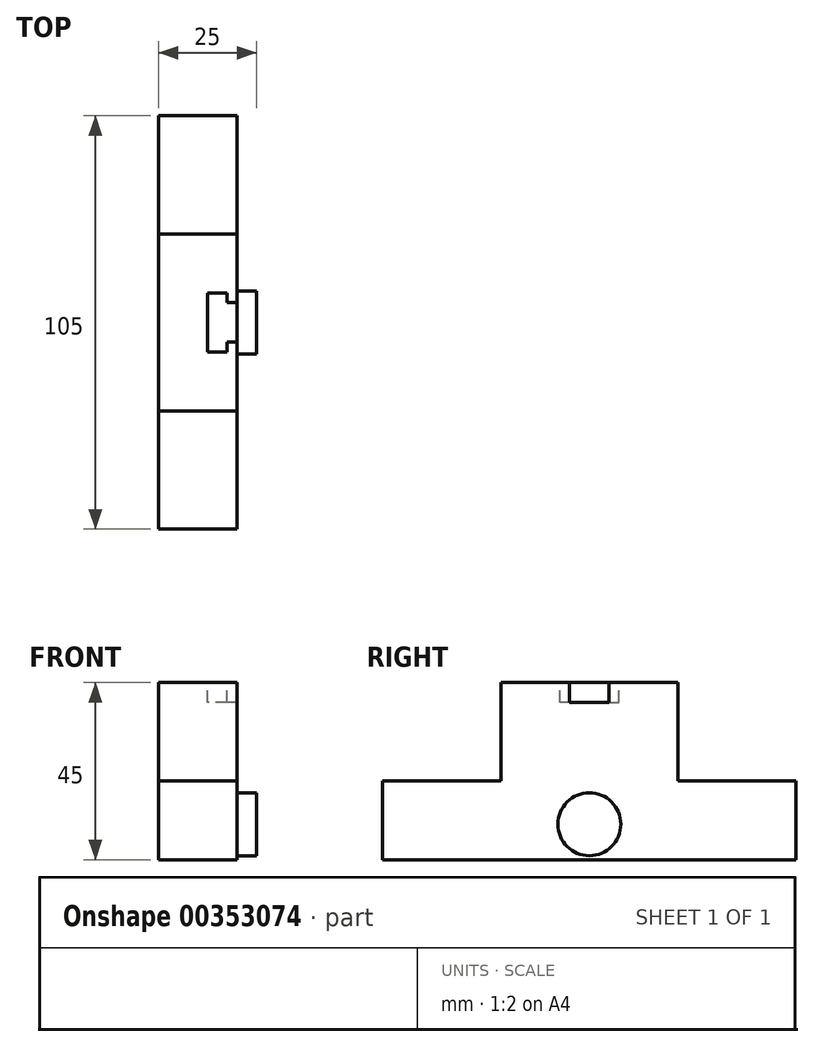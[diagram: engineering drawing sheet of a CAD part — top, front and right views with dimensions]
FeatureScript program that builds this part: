
annotation { "Feature Type Name" : "Feature", "Feature Type Description" : "" }
export const myFeature = defineFeature(function(context is Context, id is Id, definition is map)
    precondition{}
    {
        {
            var Q0;
            Q0=qCreatedBy(makeId("Top.planeOp"),FACE);
            var sketch = newSketch(context, id + "F0", { "sketchPlane" : qUnion([Q0])});
            skLineSegment(sketch, "E0.bottom", {"start": v(0, 0) * mm, "end": v(-20, 0) * mm});
            skLineSegment(sketch, "E0.top", {"start": v(0, 45) * mm, "end": v(-20, 45) * mm});
            skLineSegment(sketch, "E0.left", {"start": v(0, 0) * mm, "end": v(0, 45) * mm});
            skLineSegment(sketch, "E0.right", {"start": v(-20, 0) * mm, "end": v(-20, 45) * mm});
            skSolve(sketch);
        }
        {
            var Q0;
            Q0=makeQuery(id+"F0.imprint","IMPRINT",FACE,{"disambiguationData":[TD([[makeQuery(id+"F0.imprint","IMPRINT",EDGE,{"derivedFrom":sQuery(id+"F0.wireOp",EDGE,"E0.bottom")}),-1.0]])]});
            extrude(context, id + "F1", {"entities" : qUnion([Q0]), "depth" : 45 * mm});
        }
        {
            var Q0;
            Q0=makeQuery(id+"F1.opExtrude","CAP_FACE",FACE,{"disambiguationData":[OSD([sQuery(id+"F0.wireOp",EDGE,"E0.bottom"),sQuery(id+"F0.wireOp",EDGE,"E0.top"),sQuery(id+"F0.wireOp",EDGE,"E0.left"),sQuery(id+"F0.wireOp",EDGE,"E0.right")])],"isStart":false});
            var sketch = newSketch(context, id + "F2", { "sketchPlane" : qUnion([Q0])});
            skLineSegment(sketch, "E1", {"start": v(0, 22.5) * mm, "end": v(-20, 22.5) * mm, "construction": true});
            skLineSegment(sketch, "E2", {"start": v(0, 22.5) * mm, "end": v(0, 27.5) * mm, "construction": true});
            skLineSegment(sketch, "E3", {"start": v(0, 27.5) * mm, "end": v(-2.5, 27.5) * mm});
            skLineSegment(sketch, "E4", {"start": v(-2.5, 27.5) * mm, "end": v(-2.5, 30) * mm});
            skLineSegment(sketch, "E5", {"start": v(-2.5, 30) * mm, "end": v(-7.5, 30) * mm});
            skLineSegment(sketch, "E6", {"start": v(-7.5, 30) * mm, "end": v(-7.5, 15) * mm});
            skLineSegment(sketch, "E7", {"start": v(-7.5, 15) * mm, "end": v(-2.5, 15) * mm});
            skLineSegment(sketch, "E8", {"start": v(-2.5, 15) * mm, "end": v(-2.5, 17.5) * mm});
            skLineSegment(sketch, "E9", {"start": v(-2.5, 17.5) * mm, "end": v(0, 17.5) * mm});
            skSolve(sketch);
        }
        {
            var Q0;
            {var subQ0=sQuery(id+"F2.wireOp",EDGE,"E3");Q0=makeQuery(id+"F2.imprint","IMPRINT",FACE,{"disambiguationData":[TD([[makeQuery(id+"F2.imprint","IMPRINT",EDGE,{"derivedFrom":subQ0}),1.0]])]});}
            extrude(context, id + "F3", {"entities" : qUnion([Q0]), "operationType" : NewBodyOperationType.REMOVE, "oppositeDirection" : true, "depth" : 5 * mm});
        }
        {
            var Q0;
            Q0=makeQuery(id+"F1.opExtrude","SWEPT_FACE",FACE,{"disambiguationData":[OSD([sQuery(id+"F0.wireOp",EDGE,"E0.left")])]});
            var sketch = newSketch(context, id + "F4", { "sketchPlane" : qUnion([Q0])});
            skPoint(sketch, "E10.endSnap0", {"position": v(22.5, 0) * mm});
            skLineSegment(sketch, "E11", {"start": v(22.5, 0) * mm, "end": v(22.5, 9) * mm, "construction": true});
            skCircle(sketch, "E12", {"center": v(22.5, 9) * mm, "radius": 8 * mm});
            skSolve(sketch);
        }
        {
            var Q0;
            Q0=makeQuery(id+"F4.imprint","IMPRINT",FACE,{"disambiguationData":[TD([[makeQuery(id+"F4.imprint","IMPRINT",EDGE,{"derivedFrom":sQuery(id+"F4.wireOp",EDGE,"E12")}),1.0]])]});
            extrude(context, id + "F5", {"entities" : qUnion([Q0]), "operationType" : NewBodyOperationType.ADD, "depth" : 5 * mm});
        }
        {
            var Q0;
            Q0=makeQuery(id+"F1.opExtrude","SWEPT_FACE",FACE,{"disambiguationData":[OSD([sQuery(id+"F0.wireOp",EDGE,"E0.bottom")])]});
            var sketch = newSketch(context, id + "F6", { "sketchPlane" : qUnion([Q0])});
            skLineSegment(sketch, "E13", {"start": v(0, 0) * mm, "end": v(0, 20) * mm});
            skLineSegment(sketch, "E14", {"start": v(0, 20) * mm, "end": v(-20, 20) * mm});
            skLineSegment(sketch, "E15", {"start": v(-20, 20) * mm, "end": v(-20, 0) * mm});
            skLineSegment(sketch, "E16", {"start": v(-20, 0) * mm, "end": v(0, 0) * mm});
            skSolve(sketch);
        }
        {
            var Q0;
            Q0=makeQuery(id+"F6.imprint","IMPRINT",FACE,{"disambiguationData":[TD([[makeQuery(id+"F6.imprint","IMPRINT",EDGE,{"derivedFrom":sQuery(id+"F6.wireOp",EDGE,"E13")}),-1.0]])]});
            extrude(context, id + "F7", {"entities" : qUnion([Q0]), "operationType" : NewBodyOperationType.ADD, "depth" : 30 * mm});
        }
        {
            var Q0;
            Q0=makeQuery(id+"F1.opExtrude","SWEPT_FACE",FACE,{"disambiguationData":[OSD([sQuery(id+"F0.wireOp",EDGE,"E0.top")])]});
            var sketch = newSketch(context, id + "F8", { "sketchPlane" : qUnion([Q0])});
            skLineSegment(sketch, "E17", {"start": v(0, 0) * mm, "end": v(20, 0) * mm});
            skLineSegment(sketch, "E18", {"start": v(20, 0) * mm, "end": v(20, 20) * mm});
            skLineSegment(sketch, "E19", {"start": v(20, 20) * mm, "end": v(0, 20) * mm});
            skLineSegment(sketch, "E20", {"start": v(0, 20) * mm, "end": v(0, 0) * mm});
            skSolve(sketch);
        }
        {
            var Q0;
            Q0=makeQuery(id+"F8.imprint","IMPRINT",FACE,{"disambiguationData":[TD([[makeQuery(id+"F8.imprint","IMPRINT",EDGE,{"derivedFrom":sQuery(id+"F8.wireOp",EDGE,"E17")}),1.0]])]});
            extrude(context, id + "F9", {"entities" : qUnion([Q0]), "operationType" : NewBodyOperationType.ADD, "depth" : 30 * mm});
        }
    });
